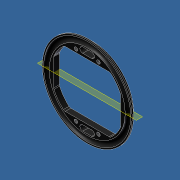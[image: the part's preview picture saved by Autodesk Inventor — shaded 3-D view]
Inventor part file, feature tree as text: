
AUTODESK INVENTOR PART (.ipt)
format: ipt  version: unknown  size: 301,568 bytes
history: native  units: in
note: dims shown in document units (in); Inventor stores cm internally (conversion verified against a paired STEP export)
features: sketch x7, extrude x5, revolve x1, hole x1, chamfer x1, fillet x1
ambient origin geometry x8: Origin, YZ Plane, XZ Plane, XY Plane, X Axis, Y Axis, Z Axis, Center Point
bodies: Solid1 (feature_tree)
feature tree (16):
  extrude  "Extrusion1"  Depth=0.25in TaperAngle=0.0deg
  extrude  "Extrusion2"  Depth=0.25in TaperAngle=0.0deg
  revolve  "Revolution1"  [1 undecoded]
  extrude  "Extrusion3"  Depth=1.25in
  extrude  "Extrusion4"  Depth=0.25in TaperAngle=0.0deg
  hole  "Hole1"  [1 undecoded]
  chamfer  "Chamfer1"  Distance=0.4673in
  fillet  "Fillet1"  Radius=0.25in
  extrude  "Extrusion5"  Depth=0.5in
  sketch  "Sketch1"  dims[d0=4.0in d1=0.25in d2=0.0in]
  sketch  "Sketch2"  dims[d3=3.2269in d4=0.25in d5=0.0in]
  sketch  "Sketch3"  dims[d6=1.8125in d7=0.025in]
  sketch  "Sketch4"  dims[d8=90.0deg d9=1.25in]
  sketch  "Sketch5"  dims[d10=1.25in d11=0.25in d12=0.0in]
  sketch  "Sketch6"  dims[d13=0.4673in d14=0.4673in]
  sketch  "Sketch7"  dims[d15=0.4673in d16=0.4673in d17=0.25in d18=0.0in d19=0.5in d20=0.5in d21=0.5in d22=0.5in d23=0.1406in d24=0.1406in d25=0.1406in d26=0.1406in d27=0.156in d28=0.75in d29=0.385in d30=0.25in d31=0.5635in d32=1.0in d33=0.8108in d34=0.1875in d35=0.125in d36=45.0deg d37=0.125in d38=0.125in d39=0.25in d40=0.175in d41=0.175in d42=0.125in d43=0.25in d44=0.125in d45=0.3in d46=0.125in d47=1.0in d48=0.0in]
note: 2 required parameter values undecoded (feature->parameter linkage not recoverable at this tier; creation-order binding heuristic only, values carry confidence <= 0.55)